# Revit family: FU_Stool_Sandler_VARYA_4-1
name_source: partatom
category: Furniture
units: mm (PartAtom-declared; Revit-internal decimal feet)

## family parameters
Always vertical = No
Cut with Voids When Loaded = No
OmniClass Number = 23.21.23.15.17
Room Calculation Point = No
Shared = No
Work Plane-Based = Yes

## types (2) — shared parameters
401D = No
401G = No
BIMobject category = Chair
BIMobject category code = furniture-chair
BIMobject main category = Furniture
BIMobject main category code = furniture
Brand url = https://www.sandlerseating.com
Default Elevation = 1219.2 mm  [stored 4 ft]
Design country = Brasil
Edition number = 1
Frame = BS18
Frame Material = Metal - Chrome - Polished
Height Frame = 770 mm  [stored 2.52625 ft]
IFC Classification = Furnishing Element
Manufacturer = Sandler
Manufacturer country = USA
Manufacturer name = Sandler
Masterformat 2014 Code = 12 48 43.13
Masterformat 2014 Description = Chair Mats
OmniClass Code = 23-21 23 15 17
Product Guid = ??
Product SKU = ??
Product data url = https://www.sandlerseating.com
Product family = Furniture
Product group = Chair
QR code = https://www.sandlerseating.com
Uniformat II Description = Movable Furnishings

## per-type parameters (varying)
| type | Description | Product name | Seat Material | Shell | Shell Material | URL | width |
| VARYA 3.1 PP | Chair | VARYA 3.1 PP | <By Category> | TP03 | <By Category> |  | 560 mm |
| VARYA 4.1 | Four-leg counter stool on a steel base, with upholstered seat and polypropylene back. Greenguard Certified. | VARYA 3.1 | Fabric - Gravity - Sunni CPC20 | TP04 | Polypropylene - M2_B44 | https://www.sandlerseating.com | 455 mm |

note: column(s) folded — value = type name in every type: Model

note: [stored X ft] marks values corroborated as IEEE doubles in the binary element streams (Revit-internal decimal feet)

## geometry (parser evidence)
native form markers: Sweep x26
no freeform markers — native parametric forms only
